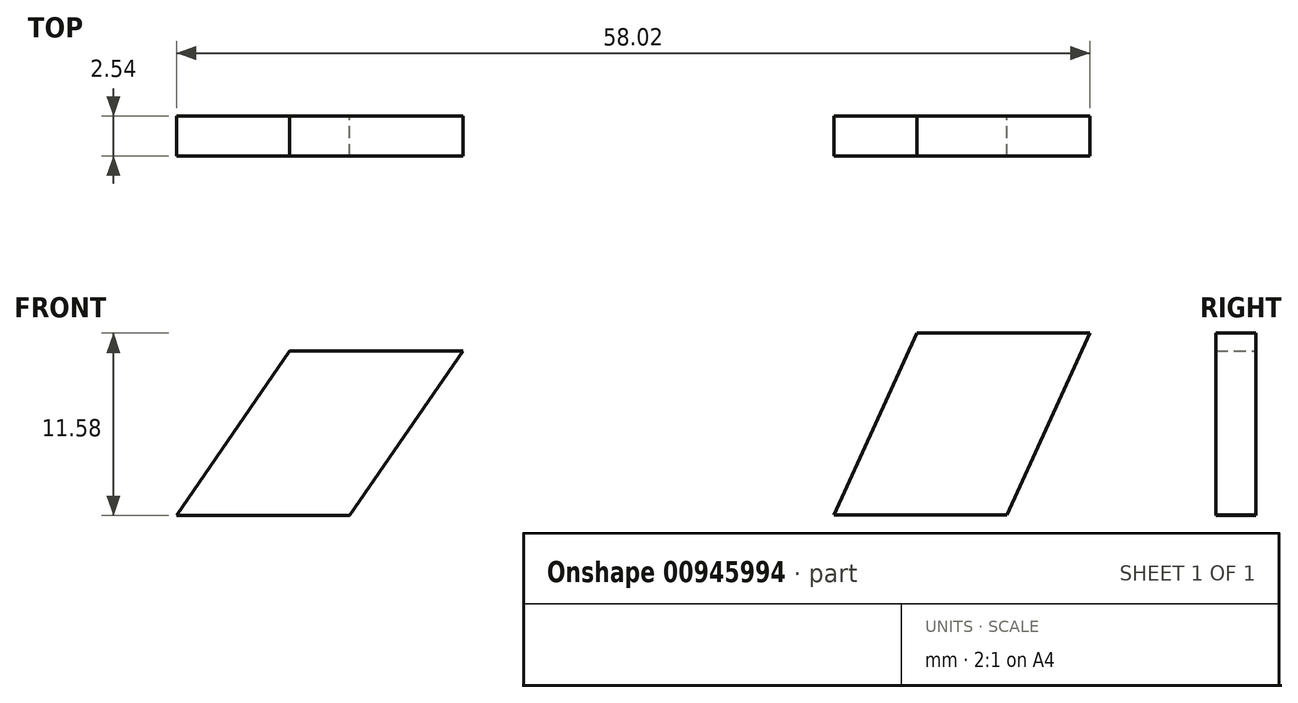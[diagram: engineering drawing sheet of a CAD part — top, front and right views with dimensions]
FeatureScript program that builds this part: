
annotation { "Feature Type Name" : "Feature", "Feature Type Description" : "" }
export const myFeature = defineFeature(function(context is Context, id is Id, definition is map)
    precondition{}
    {
        {
            var Q0;
            Q0=qCreatedBy(makeId("Front.planeOp"),FACE);
            var sketch = newSketch(context, id + "F0", { "sketchPlane" : qUnion([Q0])});
            skLineSegment(sketch, "E0", {"start": v(-31.34, 25.88) * mm, "end": v(-24.14, 36.34) * mm});
            skLineSegment(sketch, "E1", {"start": v(-24.14, 36.34) * mm, "end": v(-13.14, 36.34) * mm});
            skLineSegment(sketch, "E2", {"start": v(-13.14, 36.34) * mm, "end": v(-20.34, 25.88) * mm});
            skLineSegment(sketch, "E3", {"start": v(-20.34, 25.88) * mm, "end": v(-31.34, 25.88) * mm});
            skSolve(sketch);
        }
        {
            var Q0;
            Q0=qCreatedBy(makeId("Front.planeOp"),FACE);
            var sketch = newSketch(context, id + "F1", { "sketchPlane" : qUnion([Q0])});
            skLineSegment(sketch, "E4", {"start": v(15.68, 37.46) * mm, "end": v(26.68, 37.46) * mm});
            skLineSegment(sketch, "E5", {"start": v(26.68, 37.46) * mm, "end": v(21.43, 25.9) * mm});
            skLineSegment(sketch, "E6", {"start": v(21.43, 25.9) * mm, "end": v(10.43, 25.9) * mm});
            skLineSegment(sketch, "E7", {"start": v(10.43, 25.9) * mm, "end": v(15.68, 37.46) * mm});
            skSolve(sketch);
        }
        {
            var Q0;
            Q0=makeQuery(id+"F0.imprint","IMPRINT",FACE,{"disambiguationData":[TD([[makeQuery(id+"F0.imprint","IMPRINT",EDGE,{"derivedFrom":sQuery(id+"F0.wireOp",EDGE,"E0")}),-1.0]])]});
            extrude(context, id + "F2", {"entities" : qUnion([Q0]), "depth" : 2.54 * mm, "offsetDistance" : 25.4 * mm, "symmetric" : true});
        }
        {
            var Q0;
            Q0=makeQuery(id+"F1.imprint","IMPRINT",FACE,{"disambiguationData":[TD([[makeQuery(id+"F1.imprint","IMPRINT",EDGE,{"derivedFrom":sQuery(id+"F1.wireOp",EDGE,"E4")}),-1.0]])]});
            extrude(context, id + "F3", {"entities" : qUnion([Q0]), "depth" : 2.54 * mm, "offsetDistance" : 25.4 * mm, "symmetric" : true});
        }
    });
